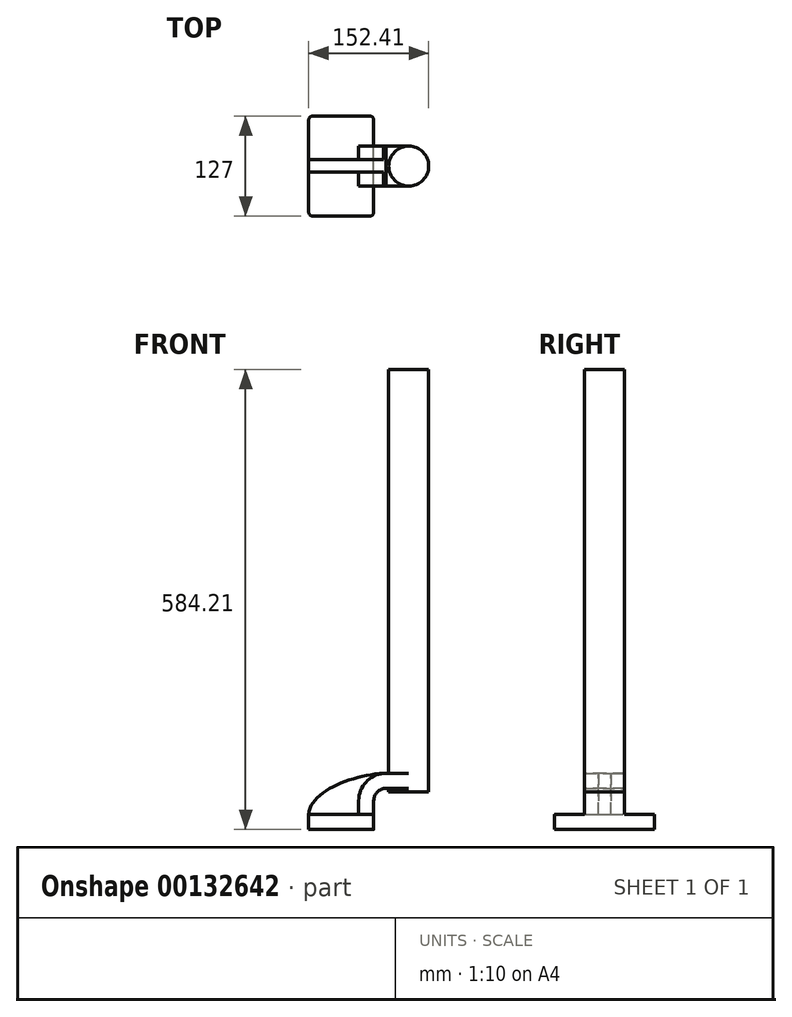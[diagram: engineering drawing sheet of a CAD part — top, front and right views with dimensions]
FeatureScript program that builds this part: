
annotation { "Feature Type Name" : "Feature", "Feature Type Description" : "" }
export const myFeature = defineFeature(function(context is Context, id is Id, definition is map)
    precondition{}
    {
        {
            var Q0;
            Q0=qCreatedBy(makeId("Front.planeOp"),FACE);
            var sketch = newSketch(context, id + "F0", { "sketchPlane" : qUnion([Q0])});
            skLineSegment(sketch, "E0.rect.bottom", {"start": v(-41.28, 9.52) * mm, "end": v(41.28, 9.52) * mm});
            skLineSegment(sketch, "E0.rect.top", {"start": v(-41.28, -9.52) * mm, "end": v(41.28, -9.52) * mm});
            skLineSegment(sketch, "E0.rect.left", {"start": v(-41.28, 9.52) * mm, "end": v(-41.28, -9.52) * mm});
            skLineSegment(sketch, "E0.rect.right", {"start": v(41.28, 9.52) * mm, "end": v(41.28, -9.52) * mm});
            skPoint(sketch, "E0.rect.middle", {"position": v(0, 0) * mm});
            skLineSegment(sketch, "E1", {"start": v(41.28, 9.52) * mm, "end": v(41.28, 27) * mm});
            skArc(sketch, "E2", {"start": v(41.28, 27) * mm, "mid": v(45.92, 38.23) * mm, "end": v(57.15, 42.88) * mm});
            skLineSegment(sketch, "E3", {"start": v(57.15, 42.88) * mm, "end": v(85.72, 42.88) * mm});
            skLineSegment(sketch, "E4.rect.bottom", {"start": v(60.32, 38.1) * mm, "end": v(111.12, 38.1) * mm});
            skLineSegment(sketch, "E4.rect.top", {"start": v(60.32, 66.68) * mm, "end": v(111.12, 66.68) * mm});
            skLineSegment(sketch, "E4.rect.left", {"start": v(60.32, 38.1) * mm, "end": v(60.32, 66.68) * mm});
            skLineSegment(sketch, "E4.rect.right", {"start": v(111.13, 38.1) * mm, "end": v(111.12, 66.68) * mm});
            skPoint(sketch, "E4.rect.middle", {"position": v(85.72, 52.39) * mm});
            skLineSegment(sketch, "E5.0", {"start": v(57.15, 61.93) * mm, "end": v(85.72, 61.93) * mm});
            skArc(sketch, "E5.1", {"start": v(22.23, 27) * mm, "mid": v(32.45, 51.7) * mm, "end": v(57.15, 61.93) * mm});
            skLineSegment(sketch, "E5.2", {"start": v(22.23, 9.52) * mm, "end": v(22.23, 27) * mm});
            skLineSegment(sketch, "E6", {"start": v(85.72, 38.1) * mm, "end": v(85.72, 66.68) * mm});
            skFitSpline(sketch, "E7", {"points": [v(-41.28, 9.53) * mm, v(57.15, 61.93) * mm], "startDerivative": vector(5.2, 92.34) * mm, "endDerivative": vector(120.92, 4.22) * mm});
            skSolve(sketch);
        }
        {
            var Q0;
            Q0=makeQuery(id+"F0.imprint","IMPRINT",FACE,{"disambiguationData":[TD([[makeQuery(id+"F0.imprint","IMPRINT",EDGE,{"derivedFrom":sQuery(id+"F0.wireOp",EDGE,"E0.rect.top")}),1.0]])]});
            extrude(context, id + "F1", {"entities" : qUnion([Q0]), "depth" : 127 * mm, "symmetric" : true});
        }
        {
            var Q0;
            {var subQ9=sQuery(id+"F0.wireOp",EDGE,"E1");Q0=makeQuery(id+"F0.imprint","IMPRINT",FACE,{"disambiguationData":[TD([[makeQuery(id+"F0.imprint","IMPRINT",EDGE,{"derivedFrom":subQ9}),1.0]])]});}
            var Q1;
            {var subQ0=sQuery(id+"F0.wireOp",EDGE,"E6");var subQ1=sQuery(id+"F0.wireOp",EDGE,"E3");var subQ2=makeQuery(id+"F0.imprint","INTERSECT",VERTEX,{"derivedFrom":[subQ1,subQ0]});Q1=makeQuery(id+"F0.imprint","IMPRINT",FACE,{"disambiguationData":[TD([[makeQuery(id+"F0.imprint","IMPRINT",EDGE,{"disambiguationData":[TD([[subQ2,1.0]])],"derivedFrom":subQ1}),1.0]])]});}
            extrude(context, id + "F2", {"entities" : qUnion([Q0, Q1]), "operationType" : NewBodyOperationType.ADD, "depth" : 50.8 * mm, "symmetric" : true});
        }
        {
            var Q0;
            {var subQ3=sQuery(id+"F0.wireOp",EDGE,"E5.2");Q0=makeQuery(id+"F0.imprint","IMPRINT",FACE,{"disambiguationData":[TD([[makeQuery(id+"F0.imprint","IMPRINT",EDGE,{"derivedFrom":subQ3}),1.0]])]});}
            extrude(context, id + "F3", {"entities" : qUnion([Q0]), "operationType" : NewBodyOperationType.ADD, "depth" : 15.88 * mm, "symmetric" : true});
        }
        {
            var Q0;
            {var subQ5=sQuery(id+"F0.wireOp",EDGE,"E4.rect.right");Q0=makeQuery(id+"F0.imprint","IMPRINT",FACE,{"disambiguationData":[TD([[makeQuery(id+"F0.imprint","IMPRINT",EDGE,{"derivedFrom":subQ5}),1.0]])]});}
            var Q1;
            Q1=sQuery(id+"F0.wireOp",EDGE,"E6");
            revolve(context, id + "F4", {"operationType" : NewBodyOperationType.ADD, "entities" : qUnion([Q0]), "axis" : qUnion([Q1]), "revolveType" : RevolveType.FULL});
        }
        {
            var Q0;
            Q0=makeQuery(id+"F1.opExtrude","CAP_EDGE",EDGE,{"disambiguationData":[OSD([sQuery(id+"F0.wireOp",EDGE,"E0.rect.right")])],"isStart":false});
            var Q1;
            Q1=makeQuery(id+"F1.opExtrude","CAP_EDGE",EDGE,{"disambiguationData":[OSD([sQuery(id+"F0.wireOp",EDGE,"E0.rect.left")])],"isStart":false});
            var Q2;
            Q2=makeQuery(id+"F1.opExtrude","CAP_EDGE",EDGE,{"disambiguationData":[OSD([sQuery(id+"F0.wireOp",EDGE,"E0.rect.right")])],"isStart":true});
            var Q3;
            Q3=makeQuery(id+"F1.opExtrude","CAP_EDGE",EDGE,{"disambiguationData":[OSD([sQuery(id+"F0.wireOp",EDGE,"E0.rect.left")])],"isStart":true});
            fillet(context, id + "F5", {"entities" : qUnion([Q0, Q1, Q2, Q3]), "radius" : 5.08 * mm, "tangentPropagation" : true, "allowEdgeOverflow" : false});
        }
        {
            var Q0;
            Q0=makeQuery(id+"F4.opRevolve","SWEPT_FACE",FACE,{"disambiguationData":[OSD([sQuery(id+"F0.wireOp",EDGE,"E4.rect.top")])]});
            extrude(context, id + "F6", {"entities" : qUnion([Q0]), "operationType" : NewBodyOperationType.ADD, "depth" : 508 * mm});
        }
    });
